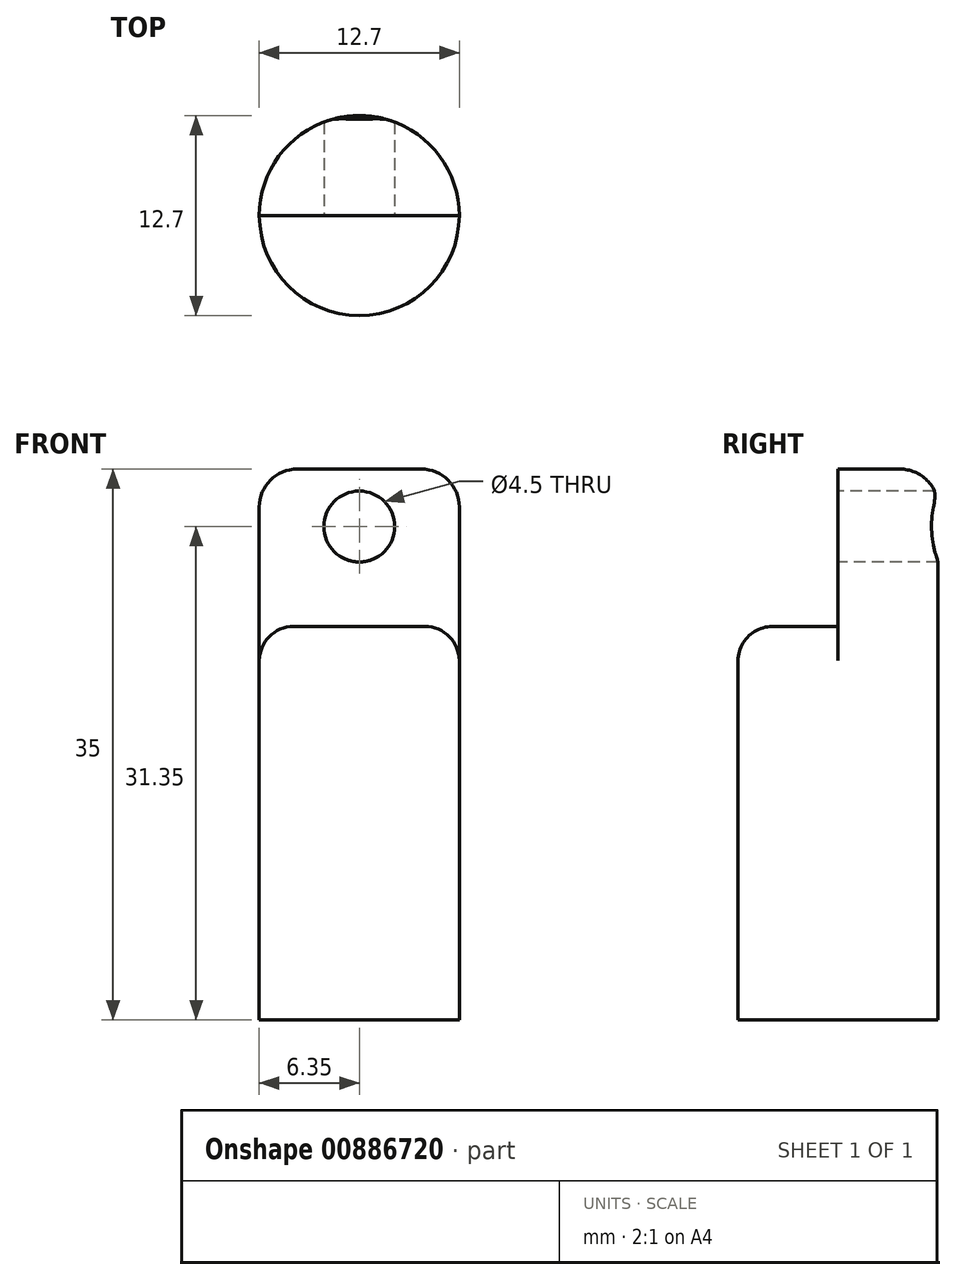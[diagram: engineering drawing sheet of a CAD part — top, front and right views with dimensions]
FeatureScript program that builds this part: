
annotation { "Feature Type Name" : "Feature", "Feature Type Description" : "" }
export const myFeature = defineFeature(function(context is Context, id is Id, definition is map)
    precondition{}
    {
        {
            var Q0;
            Q0=qCreatedBy(makeId("Top.planeOp"),FACE);
            var sketch = newSketch(context, id + "F0", { "sketchPlane" : qUnion([Q0])});
            skCircle(sketch, "E0", {"center": v(0, 0) * mm, "radius": 6.35 * mm});
            skSolve(sketch);
        }
        {
            var Q0;
            Q0 = qSketchRegion(id + "F0", true);
            extrude(context, id + "F1", {"entities" : qUnion([Q0]), "depth" : 25 * mm, "offsetDistance" : 25 * mm});
        }
        {
            var Q0;
            Q0=makeQuery(id+"F1.opExtrude","CAP_FACE",FACE,{"disambiguationData":[OSD([sQuery(id+"F0.wireOp",EDGE,"E0")])],"isStart":false});
            var sketch = newSketch(context, id + "F2", { "sketchPlane" : qUnion([Q0])});
            skArc(sketch, "E1", {"start": v(6.35, 0) * mm, "mid": v(0, 6.35) * mm, "end": v(-6.35, 0) * mm});
            skLineSegment(sketch, "E2", {"start": v(-6.35, 0) * mm, "end": v(6.35, 0) * mm});
            skSolve(sketch);
        }
        {
            var Q0;
            Q0 = qSketchRegion(id + "F2", true);
            extrude(context, id + "F3", {"entities" : qUnion([Q0]), "operationType" : NewBodyOperationType.ADD, "depth" : 12.7 * mm, "offsetDistance" : 25 * mm});
        }
        {
            var Q0;
            Q0=makeQuery(id+"F3.opExtrude","SWEPT_FACE",FACE,{"disambiguationData":[OSD([sQuery(id+"F2.wireOp",EDGE,"E2")])]});
            var sketch = newSketch(context, id + "F4", { "sketchPlane" : qUnion([Q0])});
            skCircle(sketch, "E3", {"center": v(0, 31.35) * mm, "radius": 2.25 * mm});
            skPoint(sketch, "E3.centerSnap0", {"position": v(-6.35, 31.35) * mm});
            skSolve(sketch);
        }
        {
            var Q0;
            Q0 = qSketchRegion(id + "F4", true);
            extrude(context, id + "F5", {"entities" : qUnion([Q0]), "operationType" : NewBodyOperationType.REMOVE, "oppositeDirection" : true, "depth" : 25 * mm, "offsetDistance" : 25 * mm});
        }
        {
            var Q0;
            Q0=makeQuery(id+"F3.opExtrude","CAP_FACE",FACE,{"disambiguationData":[OSD([sQuery(id+"F2.wireOp",EDGE,"E1"),sQuery(id+"F2.wireOp",EDGE,"E2")])],"isStart":false});
            var sketch = newSketch(context, id + "F6", { "sketchPlane" : qUnion([Q0])});
            skLineSegment(sketch, "E4.bottom", {"start": v(9.15, -1.4) * mm, "end": v(-9.15, -1.4) * mm});
            skLineSegment(sketch, "E4.top", {"start": v(9.15, 8.33) * mm, "end": v(-9.15, 8.33) * mm});
            skLineSegment(sketch, "E4.left", {"start": v(9.15, -1.4) * mm, "end": v(9.15, 8.33) * mm});
            skLineSegment(sketch, "E4.right", {"start": v(-9.15, -1.4) * mm, "end": v(-9.15, 8.33) * mm});
            skPoint(sketch, "E4.middle", {"position": v(0, 3.46) * mm});
            skSolve(sketch);
        }
        {
            var Q0;
            Q0 = qSketchRegion(id + "F6", true);
            extrude(context, id + "F7", {"entities" : qUnion([Q0]), "operationType" : NewBodyOperationType.REMOVE, "oppositeDirection" : true, "depth" : 2.7 * mm, "offsetDistance" : 25 * mm});
        }
        {
            var Q0;
            Q0=makeQuery(id+"F7.boolean.opBoolean","INTERSECT",EDGE,{"derivedFrom":[makeQuery(id+"F3.boolean.opBoolean","MERGE",FACE,{"derivedFrom":[makeQuery(id+"F1.opExtrude","SWEPT_FACE",FACE,{"disambiguationData":[OSD([sQuery(id+"F0.wireOp",EDGE,"E0")])]}),makeQuery(id+"F3.opExtrude","SWEPT_FACE",FACE,{"disambiguationData":[OSD([sQuery(id+"F2.wireOp",EDGE,"E1")])]})]}),makeQuery(id+"F7.opExtrude","CAP_FACE",FACE,{"disambiguationData":[OSD([sQuery(id+"F6.wireOp",EDGE,"E4.bottom"),sQuery(id+"F6.wireOp",EDGE,"E4.top"),sQuery(id+"F6.wireOp",EDGE,"E4.left"),sQuery(id+"F6.wireOp",EDGE,"E4.right")])],"isStart":false})]});
            fillet(context, id + "F8", {"entities" : qUnion([Q0]), "radius" : 2.41 * mm, "tangentPropagation" : true, "allowEdgeOverflow" : false});
        }
        {
            var Q0;
            Q0=makeQuery(id+"F1.opExtrude","CAP_EDGE",EDGE,{"disambiguationData":[OSD([sQuery(id+"F0.wireOp",EDGE,"E0")])],"isStart":false});
            fillet(context, id + "F9", {"entities" : qUnion([Q0]), "radius" : 2.17 * mm, "tangentPropagation" : true, "allowEdgeOverflow" : false});
        }
    });
